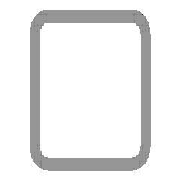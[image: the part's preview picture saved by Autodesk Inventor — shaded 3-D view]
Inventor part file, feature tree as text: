
AUTODESK INVENTOR PART (.ipt)
format: ipt  version: 2025.1 (Build 291241020, 241B)  size: 134,144 bytes
history: native  units: mm (DEFAULTED — no unit token found)
features: other x4, sketch x1, plane x1
ambient origin geometry x8: Origin, YZ Plane, XZ Plane, XY Plane, X Axis, Y Axis, Z Axis, Center Point
bodies: Solid1 (feature_tree), Body (feature_tree)
feature tree (6):
  parser-record x1  (decoder bookkeeping rows leaked as tree rows — omitted from the tree; the rows remain in map.json)
  other  "Driven Length"
  other  "Start plane"
  other  "End plane"
  sketch  "Sketch3"  dims[d3=2750.0mm d4=0.0mm d7=6.0mm d9=60.0mm d11=60.0mm d12=3.0mm d13=-0.0mm d14=2750.0mm d15=30.0mm d16=30.0mm d17=90.0deg d18=2750.0mm]
  plane  "Work Plane3"
